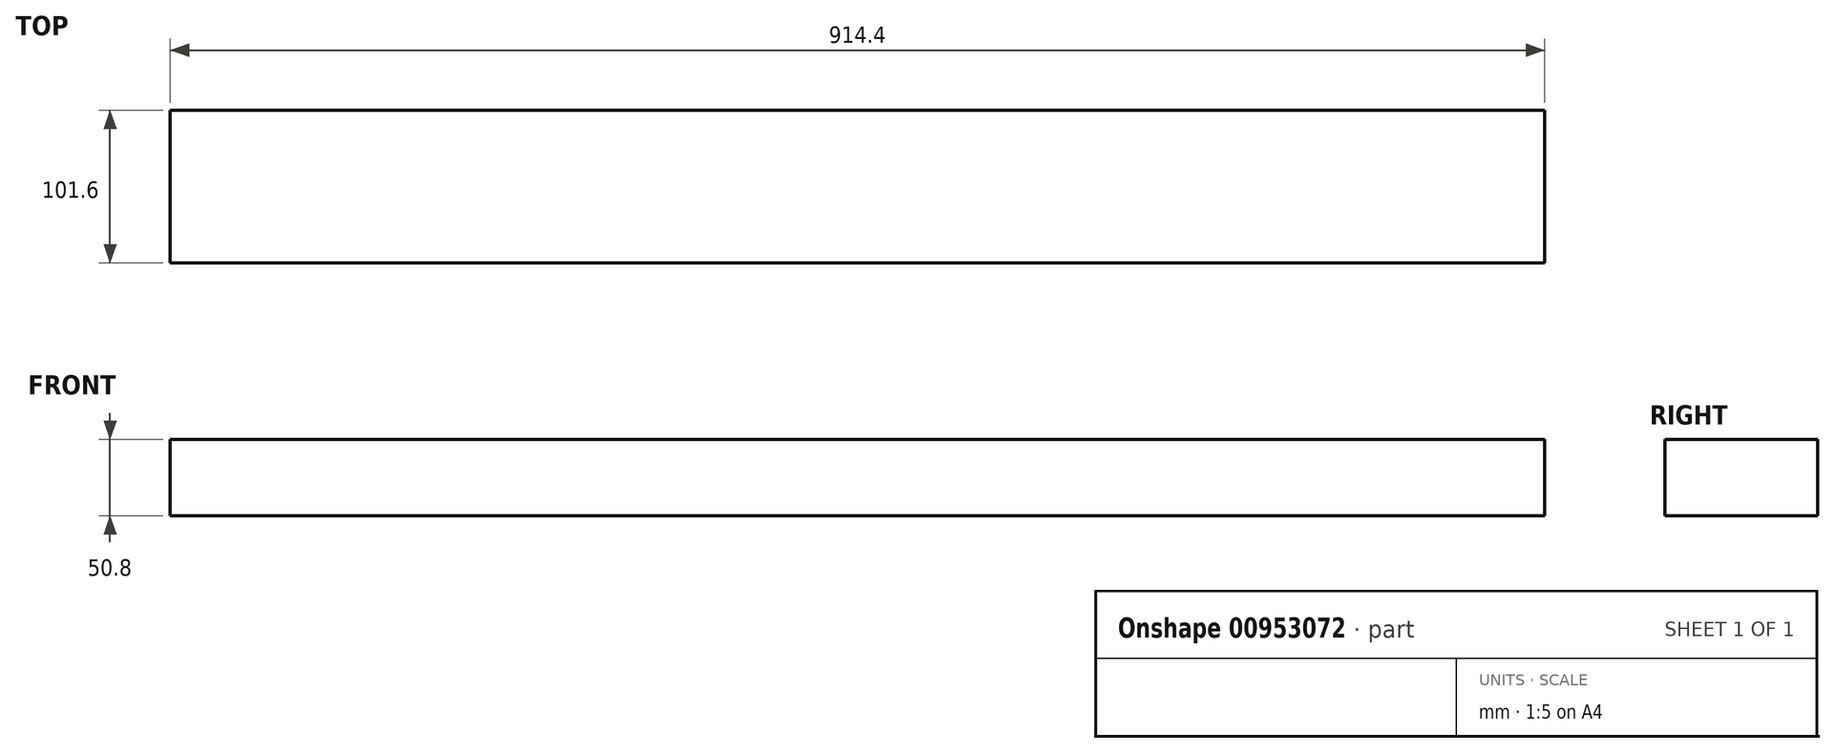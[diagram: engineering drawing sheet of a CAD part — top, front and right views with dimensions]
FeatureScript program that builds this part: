
annotation { "Feature Type Name" : "Feature", "Feature Type Description" : "" }
export const myFeature = defineFeature(function(context is Context, id is Id, definition is map)
    precondition{}
    {
        {
            var Q0;
            Q0=qCreatedBy(makeId("Top.planeOp"),FACE);
            var sketch = newSketch(context, id + "F0", { "sketchPlane" : qUnion([Q0])});
            skLineSegment(sketch, "E0", {"start": v(0, 0) * mm, "end": v(-914.4, 0) * mm});
            skLineSegment(sketch, "E1", {"start": v(-914.4, 0) * mm, "end": v(-914.4, 101.6) * mm});
            skLineSegment(sketch, "E2", {"start": v(-914.4, 101.6) * mm, "end": v(0, 101.6) * mm});
            skLineSegment(sketch, "E3", {"start": v(0, 101.6) * mm, "end": v(0, 0) * mm});
            skSolve(sketch);
        }
        {
            var Q0;
            Q0 = qSketchRegion(id + "F0", true);
            extrude(context, id + "F1", {"entities" : qUnion([Q0]), "depth" : 50.8 * mm, "offsetDistance" : 25.4 * mm});
        }
    });
